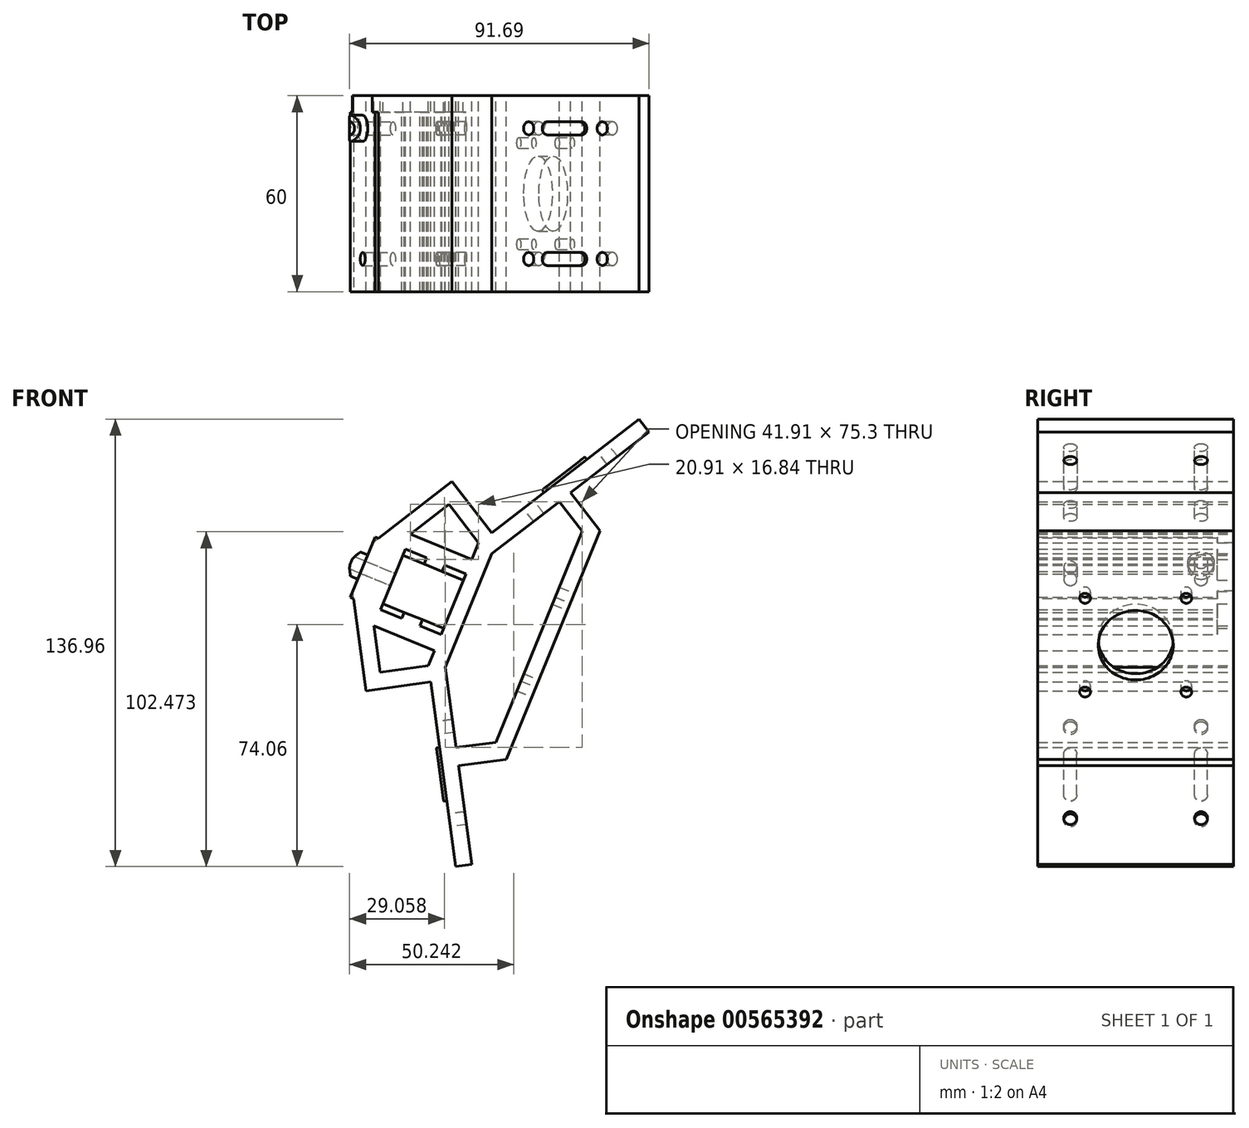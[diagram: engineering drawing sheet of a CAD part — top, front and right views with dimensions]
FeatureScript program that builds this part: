
annotation { "Feature Type Name" : "Feature", "Feature Type Description" : "" }
export const myFeature = defineFeature(function(context is Context, id is Id, definition is map)
    precondition{}
    {
        {
            var Q0;
            Q0=qCreatedBy(makeId("Front.planeOp"),FACE);
            var sketch = newSketch(context, id + "F0", { "sketchPlane" : qUnion([Q0])});
            skLineSegment(sketch, "E0", {"start": v(-32.47, 25.35) * mm, "end": v(-0.83, 49.82) * mm});
            skLineSegment(sketch, "E1", {"start": v(-0.83, 49.82) * mm, "end": v(11.4, 34) * mm});
            skLineSegment(sketch, "E2", {"start": v(-7.28, -11.6) * mm, "end": v(-27.1, -14.29) * mm});
            skLineSegment(sketch, "E3", {"start": v(-27.1, -14.29) * mm, "end": v(-32.47, 25.35) * mm});
            skLineSegment(sketch, "E4", {"start": v(11.4, 34) * mm, "end": v(56.5, 68.87) * mm});
            skLineSegment(sketch, "E5", {"start": v(56.5, 68.87) * mm, "end": v(59.56, 64.91) * mm});
            skLineSegment(sketch, "E6", {"start": v(59.56, 64.91) * mm, "end": v(11.4, 27.68) * mm});
            skLineSegment(sketch, "E7", {"start": v(11.4, 27.68) * mm, "end": v(-2.84, -7.1) * mm});
            skLineSegment(sketch, "E8", {"start": v(-2.84, -7.1) * mm, "end": v(5.33, -67.42) * mm});
            skLineSegment(sketch, "E9", {"start": v(5.33, -67.42) * mm, "end": v(0.37, -68.09) * mm});
            skLineSegment(sketch, "E10", {"start": v(0.37, -68.09) * mm, "end": v(-7.28, -11.6) * mm});
            skPoint(sketch, "E11", {"position": v(35.48, 46.3) * mm});
            skPoint(sketch, "E12", {"position": v(1.24, -37.26) * mm});
            skLineSegment(sketch, "E13", {"start": v(35.48, 46.3) * mm, "end": v(44.51, 34.62) * mm});
            skLineSegment(sketch, "E14", {"start": v(44.51, 34.62) * mm, "end": v(15.87, -35.28) * mm});
            skLineSegment(sketch, "E15", {"start": v(15.87, -35.28) * mm, "end": v(1.24, -37.26) * mm});
            skLineSegment(sketch, "E16", {"start": v(12.61, -30.04) * mm, "end": v(39.07, 34.52) * mm});
            skLineSegment(sketch, "E17", {"start": v(3.45, 21.44) * mm, "end": v(-15.06, 29.02) * mm});
            skLineSegment(sketch, "E18", {"start": v(-15.06, 29.02) * mm, "end": v(-22.64, 10.51) * mm});
            skLineSegment(sketch, "E19", {"start": v(-22.64, 10.51) * mm, "end": v(-4.14, 2.93) * mm});
            skLineSegment(sketch, "E20", {"start": v(-4.14, 2.93) * mm, "end": v(3.45, 21.44) * mm});
            skLineSegment(sketch, "E21", {"start": v(39.07, 34.52) * mm, "end": v(32.03, 43.62) * mm});
            skLineSegment(sketch, "E22", {"start": v(12.61, -30.04) * mm, "end": v(0.49, -31.68) * mm});
            skPoint(sketch, "E23", {"position": v(4.28, 10.29) * mm});
            skPoint(sketch, "E24", {"position": v(-0.34, 12.18) * mm});
            skLineSegment(sketch, "E25", {"start": v(4.28, 10.29) * mm, "end": v(-0.34, 12.18) * mm});
            skLineSegment(sketch, "E26", {"start": v(2.7, 19.59) * mm, "end": v(-15.82, 27.17) * mm});
            skLineSegment(sketch, "E27", {"start": v(-3.38, 4.78) * mm, "end": v(-21.88, 12.37) * mm});
            skLineSegment(sketch, "E28", {"start": v(-10.61, 5.59) * mm, "end": v(-9.85, 7.44) * mm});
            skLineSegment(sketch, "E29", {"start": v(-16.16, 7.86) * mm, "end": v(-15.4, 9.71) * mm});
            skLineSegment(sketch, "E30", {"start": v(-9.34, 24.52) * mm, "end": v(-8.58, 26.37) * mm});
            skPoint(sketch, "E31", {"position": v(-13.39, 6.72) * mm});
            skPoint(sketch, "E32", {"position": v(-5.8, 25.23) * mm});
            skLineSegment(sketch, "E33", {"start": v(-3.79, 22.24) * mm, "end": v(-3.03, 24.1) * mm});
            skLineSegment(sketch, "E34", {"start": v(-1.72, 42.8) * mm, "end": v(7.38, 31.03) * mm});
            skLineSegment(sketch, "E35", {"start": v(7.38, 31.03) * mm, "end": v(5.3, 25.96) * mm});
            skLineSegment(sketch, "E36", {"start": v(5.3, 25.96) * mm, "end": v(-13.52, 33.68) * mm});
            skLineSegment(sketch, "E37", {"start": v(-13.52, 33.68) * mm, "end": v(-1.72, 42.8) * mm});
            skLineSegment(sketch, "E38", {"start": v(-6.19, -2.07) * mm, "end": v(-8.07, -6.67) * mm});
            skLineSegment(sketch, "E39", {"start": v(-8.07, -6.67) * mm, "end": v(-22.81, -8.66) * mm});
            skLineSegment(sketch, "E40", {"start": v(-22.81, -8.66) * mm, "end": v(-24.74, 5.53) * mm});
            skPoint(sketch, "E40.endSnap0", {"position": v(-29.78, 5.53) * mm});
            skLineSegment(sketch, "E41", {"start": v(-24.74, 5.53) * mm, "end": v(-6.19, -2.07) * mm});
            skSolve(sketch);
        }
        {
            var Q0;
            Q0=makeQuery(id+"F0.imprint","IMPRINT",FACE,{"disambiguationData":[TD([[makeQuery(id+"F0.imprint","IMPRINT",EDGE,{"derivedFrom":sQuery(id+"F0.wireOp",EDGE,"E0")}),-1.0]])]});
            var Q1;
            {var subQ0=sQuery(id+"F0.wireOp",EDGE,"E30");Q1=makeQuery(id+"F0.imprint","IMPRINT",FACE,{"disambiguationData":[TD([[makeQuery(id+"F0.imprint","IMPRINT",EDGE,{"derivedFrom":subQ0}),-1.0]])]});}
            var Q2;
            {var subQ0=sQuery(id+"F0.wireOp",EDGE,"E28");Q2=makeQuery(id+"F0.imprint","IMPRINT",FACE,{"disambiguationData":[TD([[makeQuery(id+"F0.imprint","IMPRINT",EDGE,{"derivedFrom":subQ0}),1.0]])]});}
            var Q3;
            {var subQ0=sQuery(id+"F0.wireOp",EDGE,"E13");Q3=makeQuery(id+"F0.imprint","IMPRINT",FACE,{"disambiguationData":[TD([[makeQuery(id+"F0.imprint","IMPRINT",EDGE,{"derivedFrom":subQ0}),-1.0]])]});}
            extrude(context, id + "F1", {"entities" : qUnion([Q0, Q1, Q2, Q3]), "depth" : 60 * mm, "offsetDistance" : 25 * mm});
        }
        {
            var Q0;
            {var subQ3=sQuery(id+"F0.wireOp",EDGE,"E28");Q0=makeQuery(id+"F0.imprint","IMPRINT",FACE,{"disambiguationData":[TD([[makeQuery(id+"F0.imprint","IMPRINT",EDGE,{"derivedFrom":subQ3}),-1.0]])]});}
            var Q1;
            {var subQ5=sQuery(id+"F0.wireOp",EDGE,"E29");Q1=makeQuery(id+"F0.imprint","IMPRINT",FACE,{"disambiguationData":[TD([[makeQuery(id+"F0.imprint","IMPRINT",EDGE,{"derivedFrom":subQ5}),1.0]])]});}
            var Q2;
            {var subQ3=sQuery(id+"F0.wireOp",EDGE,"E30");Q2=makeQuery(id+"F0.imprint","IMPRINT",FACE,{"disambiguationData":[TD([[makeQuery(id+"F0.imprint","IMPRINT",EDGE,{"derivedFrom":subQ3}),1.0]])]});}
            var Q3;
            {var subQ3=sQuery(id+"F0.wireOp",EDGE,"E33");Q3=makeQuery(id+"F0.imprint","IMPRINT",FACE,{"disambiguationData":[TD([[makeQuery(id+"F0.imprint","IMPRINT",EDGE,{"derivedFrom":subQ3}),-1.0]])]});}
            extrude(context, id + "F2", {"entities" : qUnion([Q0, Q1, Q2, Q3]), "operationType" : NewBodyOperationType.ADD, "depth" : 5 * mm, "offsetDistance" : 25 * mm});
        }
        {
            var Q0;
            Q0=makeQuery(id+"F1.opExtrude","SWEPT_FACE",FACE,{"disambiguationData":[OSD([sQuery(id+"F0.wireOp",EDGE,"E14")])]});
            var sketch = newSketch(context, id + "F3", { "sketchPlane" : qUnion([Q0])});
            skCircle(sketch, "E42", {"center": v(-30, 11.14) * mm, "radius": 11.5 * mm});
            skCircle(sketch, "E43", {"center": v(-45.5, 26.64) * mm, "radius": 1.65 * mm});
            skCircle(sketch, "E44", {"center": v(-45.5, -4.36) * mm, "radius": 1.65 * mm});
            skCircle(sketch, "E45", {"center": v(-14.5, -4.36) * mm, "radius": 1.65 * mm});
            skCircle(sketch, "E46", {"center": v(-14.5, 26.64) * mm, "radius": 1.65 * mm});
            skSolve(sketch);
        }
        {
            var Q0;
            Q0=makeQuery(id+"F3.imprint","IMPRINT",FACE,{"disambiguationData":[TD([[makeQuery(id+"F3.imprint","IMPRINT",EDGE,{"derivedFrom":sQuery(id+"F3.wireOp",EDGE,"E42")}),1.0]])]});
            extrude(context, id + "F4", {"entities" : qUnion([Q0]), "operationType" : NewBodyOperationType.REMOVE, "oppositeDirection" : true, "depth" : 5 * mm, "offsetDistance" : 25 * mm});
        }
        {
            var Q0;
            Q0=makeQuery(id+"F3.imprint","IMPRINT",FACE,{"disambiguationData":[TD([[makeQuery(id+"F3.imprint","IMPRINT",EDGE,{"derivedFrom":sQuery(id+"F3.wireOp",EDGE,"E44")}),1.0]])]});
            var Q1;
            Q1=makeQuery(id+"F3.imprint","IMPRINT",FACE,{"disambiguationData":[TD([[makeQuery(id+"F3.imprint","IMPRINT",EDGE,{"derivedFrom":sQuery(id+"F3.wireOp",EDGE,"E43")}),1.0]])]});
            var Q2;
            Q2=makeQuery(id+"F3.imprint","IMPRINT",FACE,{"disambiguationData":[TD([[makeQuery(id+"F3.imprint","IMPRINT",EDGE,{"derivedFrom":sQuery(id+"F3.wireOp",EDGE,"E46")}),1.0]])]});
            var Q3;
            Q3=makeQuery(id+"F3.imprint","IMPRINT",FACE,{"disambiguationData":[TD([[makeQuery(id+"F3.imprint","IMPRINT",EDGE,{"derivedFrom":sQuery(id+"F3.wireOp",EDGE,"E45")}),1.0]])]});
            extrude(context, id + "F5", {"entities" : qUnion([Q0, Q1, Q2, Q3]), "operationType" : NewBodyOperationType.REMOVE, "oppositeDirection" : true, "depth" : 5 * mm, "offsetDistance" : 25 * mm});
        }
        {
            var Q0;
            Q0=makeQuery(id+"F1.opExtrude","SWEPT_EDGE",EDGE,{"disambiguationData":[OSD([sQuery(id+"F0.wireOp",EDGE,"E0"),sQuery(id+"F0.wireOp",EDGE,"E3")])]});
            fillet(context, id + "F6", {"entities" : qUnion([Q0]), "radius" : 5 * mm, "tangentPropagation" : true, "allowEdgeOverflow" : false});
        }
        {
            var Q0;
            Q0=makeQuery(id+"F1.opExtrude","SWEPT_FACE",FACE,{"disambiguationData":[OSD([sQuery(id+"F0.wireOp",EDGE,"E10")])]});
            var sketch = newSketch(context, id + "F7", { "sketchPlane" : qUnion([Q0])});
            skCircle(sketch, "E47", {"center": v(10, -53.27) * mm, "radius": 2 * mm});
            skCircle(sketch, "E48", {"center": v(10, -24.77) * mm, "radius": 2 * mm});
            skCircle(sketch, "E49", {"center": v(50, -24.78) * mm, "radius": 2 * mm});
            skCircle(sketch, "E50", {"center": v(50, -53.27) * mm, "radius": 2 * mm});
            skLineSegment(sketch, "E51", {"start": v(12, -53.27) * mm, "end": v(12, -24.77) * mm});
            skLineSegment(sketch, "E52", {"start": v(8, -53.27) * mm, "end": v(8, -24.77) * mm});
            skCircle(sketch, "E53", {"center": v(10, -45.27) * mm, "radius": 2 * mm});
            skCircle(sketch, "E54", {"center": v(10, -32.77) * mm, "radius": 2 * mm});
            skLineSegment(sketch, "E55", {"start": v(48, -53.27) * mm, "end": v(48, -24.78) * mm});
            skLineSegment(sketch, "E56", {"start": v(52, -53.27) * mm, "end": v(52, -24.78) * mm});
            skCircle(sketch, "E57", {"center": v(50, -45.27) * mm, "radius": 2 * mm});
            skCircle(sketch, "E58", {"center": v(50, -32.78) * mm, "radius": 2 * mm});
            skSolve(sketch);
        }
        {
            var Q0;
            Q0=makeQuery(id+"F7.imprint","IMPRINT",FACE,{"disambiguationData":[TD([[makeQuery(id+"F7.imprint","IMPRINT",EDGE,{"derivedFrom":sQuery(id+"F7.wireOp",EDGE,"E47")}),1.0]])]});
            var Q1;
            Q1=makeQuery(id+"F7.imprint","IMPRINT",FACE,{"disambiguationData":[TD([[makeQuery(id+"F7.imprint","IMPRINT",EDGE,{"derivedFrom":sQuery(id+"F7.wireOp",EDGE,"E50")}),1.0]])]});
            var Q2;
            Q2=makeQuery(id+"F7.imprint","IMPRINT",FACE,{"disambiguationData":[TD([[makeQuery(id+"F7.imprint","IMPRINT",EDGE,{"derivedFrom":sQuery(id+"F7.wireOp",EDGE,"E49")}),1.0]])]});
            var Q3;
            Q3=makeQuery(id+"F7.imprint","IMPRINT",FACE,{"disambiguationData":[TD([[makeQuery(id+"F7.imprint","IMPRINT",EDGE,{"derivedFrom":sQuery(id+"F7.wireOp",EDGE,"E48")}),1.0]])]});
            extrude(context, id + "F8", {"entities" : qUnion([Q0, Q1, Q2, Q3]), "operationType" : NewBodyOperationType.REMOVE, "oppositeDirection" : true, "depth" : 5 * mm, "offsetDistance" : 25 * mm});
        }
        {
            var Q0;
            {var subQ0=sQuery(id+"F7.wireOp",EDGE,"E57");var subQ1=makeQuery(id+"F7.imprint","INTERSECT",VERTEX,{"derivedFrom":[sQuery(id+"F7.wireOp",EDGE,"E55"),subQ0]});Q0=makeQuery(id+"F7.imprint","IMPRINT",FACE,{"disambiguationData":[TD([[makeQuery(id+"F7.imprint","IMPRINT",EDGE,{"disambiguationData":[TD([[subQ1,1.0]])],"derivedFrom":subQ0}),1.0]])]});}
            var Q1;
            {var subQ0=sQuery(id+"F7.wireOp",EDGE,"E57");var subQ1=sQuery(id+"F7.wireOp",EDGE,"E55");var subQ2=makeQuery(id+"F7.imprint","INTERSECT",VERTEX,{"derivedFrom":[subQ1,subQ0]});Q1=makeQuery(id+"F7.imprint","IMPRINT",FACE,{"disambiguationData":[TD([[makeQuery(id+"F7.imprint","IMPRINT",EDGE,{"disambiguationData":[TD([[subQ2,-1.0]])],"derivedFrom":subQ1}),-1.0]])]});}
            var Q2;
            {var subQ0=sQuery(id+"F7.wireOp",EDGE,"E58");var subQ1=makeQuery(id+"F7.imprint","INTERSECT",VERTEX,{"derivedFrom":[sQuery(id+"F7.wireOp",EDGE,"E55"),subQ0]});Q2=makeQuery(id+"F7.imprint","IMPRINT",FACE,{"disambiguationData":[TD([[makeQuery(id+"F7.imprint","IMPRINT",EDGE,{"disambiguationData":[TD([[subQ1,1.0]])],"derivedFrom":subQ0}),1.0]])]});}
            var Q3;
            {var subQ0=sQuery(id+"F7.wireOp",EDGE,"E53");var subQ1=sQuery(id+"F7.wireOp",EDGE,"E51");var subQ2=makeQuery(id+"F7.imprint","INTERSECT",VERTEX,{"derivedFrom":[subQ1,subQ0]});Q3=makeQuery(id+"F7.imprint","IMPRINT",FACE,{"disambiguationData":[TD([[makeQuery(id+"F7.imprint","IMPRINT",EDGE,{"disambiguationData":[TD([[subQ2,-1.0]])],"derivedFrom":subQ1}),1.0]])]});}
            var Q4;
            {var subQ0=sQuery(id+"F7.wireOp",EDGE,"E54");var subQ1=makeQuery(id+"F7.imprint","INTERSECT",VERTEX,{"derivedFrom":[sQuery(id+"F7.wireOp",EDGE,"E51"),subQ0]});Q4=makeQuery(id+"F7.imprint","IMPRINT",FACE,{"disambiguationData":[TD([[makeQuery(id+"F7.imprint","IMPRINT",EDGE,{"disambiguationData":[TD([[subQ1,-1.0]])],"derivedFrom":subQ0}),1.0]])]});}
            var Q5;
            {var subQ0=sQuery(id+"F7.wireOp",EDGE,"E53");var subQ1=makeQuery(id+"F7.imprint","INTERSECT",VERTEX,{"derivedFrom":[sQuery(id+"F7.wireOp",EDGE,"E51"),subQ0]});Q5=makeQuery(id+"F7.imprint","IMPRINT",FACE,{"disambiguationData":[TD([[makeQuery(id+"F7.imprint","IMPRINT",EDGE,{"disambiguationData":[TD([[subQ1,-1.0]])],"derivedFrom":subQ0}),1.0]])]});}
            extrude(context, id + "F9", {"entities" : qUnion([Q0, Q1, Q2, Q3, Q4, Q5]), "operationType" : NewBodyOperationType.ADD, "depth" : 1 * mm, "offsetDistance" : 25 * mm});
        }
        {
            var Q0;
            Q0=makeQuery(id+"F1.opExtrude","SWEPT_FACE",FACE,{"disambiguationData":[OSD([sQuery(id+"F0.wireOp",EDGE,"E4")])]});
            var sketch = newSketch(context, id + "F10", { "sketchPlane" : qUnion([Q0])});
            skCircle(sketch, "E59", {"center": v(44.07, -10) * mm, "radius": 2 * mm});
            skCircle(sketch, "E60", {"center": v(72.57, -10) * mm, "radius": 2 * mm});
            skCircle(sketch, "E61", {"center": v(72.57, -50) * mm, "radius": 2 * mm});
            skCircle(sketch, "E62", {"center": v(44.07, -50) * mm, "radius": 2 * mm});
            skLineSegment(sketch, "E63", {"start": v(44.07, -12) * mm, "end": v(72.57, -12) * mm});
            skLineSegment(sketch, "E64", {"start": v(72.57, -48) * mm, "end": v(44.07, -48) * mm});
            skLineSegment(sketch, "E65", {"start": v(44.07, -8) * mm, "end": v(72.57, -8) * mm});
            skLineSegment(sketch, "E66", {"start": v(44.07, -52) * mm, "end": v(72.57, -52) * mm});
            skCircle(sketch, "E67", {"center": v(52.07, -10) * mm, "radius": 2 * mm});
            skCircle(sketch, "E68", {"center": v(64.57, -10) * mm, "radius": 2 * mm});
            skCircle(sketch, "E69", {"center": v(52.07, -50) * mm, "radius": 2 * mm});
            skCircle(sketch, "E70", {"center": v(64.57, -50) * mm, "radius": 2 * mm});
            skSolve(sketch);
        }
        {
            var Q0;
            {var subQ0=sQuery(id+"F10.wireOp",EDGE,"E67");var subQ1=sQuery(id+"F10.wireOp",EDGE,"E63");var subQ2=makeQuery(id+"F10.imprint","INTERSECT",VERTEX,{"derivedFrom":[subQ1,subQ0]});Q0=makeQuery(id+"F10.imprint","IMPRINT",FACE,{"disambiguationData":[TD([[makeQuery(id+"F10.imprint","IMPRINT",EDGE,{"disambiguationData":[TD([[subQ2,-1.0]])],"derivedFrom":subQ1}),1.0]])]});}
            var Q1;
            {var subQ0=sQuery(id+"F10.wireOp",EDGE,"E67");var subQ1=makeQuery(id+"F10.imprint","INTERSECT",VERTEX,{"derivedFrom":[sQuery(id+"F10.wireOp",EDGE,"E63"),subQ0]});Q1=makeQuery(id+"F10.imprint","IMPRINT",FACE,{"disambiguationData":[TD([[makeQuery(id+"F10.imprint","IMPRINT",EDGE,{"disambiguationData":[TD([[subQ1,1.0]])],"derivedFrom":subQ0}),1.0]])]});}
            var Q2;
            {var subQ0=sQuery(id+"F10.wireOp",EDGE,"E68");var subQ1=makeQuery(id+"F10.imprint","INTERSECT",VERTEX,{"derivedFrom":[sQuery(id+"F10.wireOp",EDGE,"E63"),subQ0]});Q2=makeQuery(id+"F10.imprint","IMPRINT",FACE,{"disambiguationData":[TD([[makeQuery(id+"F10.imprint","IMPRINT",EDGE,{"disambiguationData":[TD([[subQ1,1.0]])],"derivedFrom":subQ0}),1.0]])]});}
            var Q3;
            {var subQ0=sQuery(id+"F10.wireOp",EDGE,"E69");var subQ1=makeQuery(id+"F10.imprint","INTERSECT",VERTEX,{"derivedFrom":[sQuery(id+"F10.wireOp",EDGE,"E64"),subQ0]});Q3=makeQuery(id+"F10.imprint","IMPRINT",FACE,{"disambiguationData":[TD([[makeQuery(id+"F10.imprint","IMPRINT",EDGE,{"disambiguationData":[TD([[subQ1,-1.0]])],"derivedFrom":subQ0}),1.0]])]});}
            var Q4;
            {var subQ0=sQuery(id+"F10.wireOp",EDGE,"E70");var subQ1=sQuery(id+"F10.wireOp",EDGE,"E64");var subQ2=makeQuery(id+"F10.imprint","INTERSECT",VERTEX,{"derivedFrom":[subQ1,subQ0]});Q4=makeQuery(id+"F10.imprint","IMPRINT",FACE,{"disambiguationData":[TD([[makeQuery(id+"F10.imprint","IMPRINT",EDGE,{"disambiguationData":[TD([[subQ2,-1.0]])],"derivedFrom":subQ1}),1.0]])]});}
            var Q5;
            {var subQ0=sQuery(id+"F10.wireOp",EDGE,"E70");var subQ1=makeQuery(id+"F10.imprint","INTERSECT",VERTEX,{"derivedFrom":[sQuery(id+"F10.wireOp",EDGE,"E64"),subQ0]});Q5=makeQuery(id+"F10.imprint","IMPRINT",FACE,{"disambiguationData":[TD([[makeQuery(id+"F10.imprint","IMPRINT",EDGE,{"disambiguationData":[TD([[subQ1,-1.0]])],"derivedFrom":subQ0}),1.0]])]});}
            extrude(context, id + "F11", {"entities" : qUnion([Q0, Q1, Q2, Q3, Q4, Q5]), "operationType" : NewBodyOperationType.ADD, "depth" : 1 * mm, "offsetDistance" : 25 * mm});
        }
        {
            var Q0;
            {var subQ0=sQuery(id+"F10.wireOp",EDGE,"E59");var subQ1=makeQuery(id+"F10.imprint","INTERSECT",VERTEX,{"derivedFrom":[subQ0,sQuery(id+"F10.wireOp",EDGE,"E63")]});Q0=makeQuery(id+"F10.imprint","IMPRINT",FACE,{"disambiguationData":[TD([[makeQuery(id+"F10.imprint","IMPRINT",EDGE,{"disambiguationData":[TD([[subQ1,1.0]])],"derivedFrom":subQ0}),1.0]])]});}
            var Q1;
            {var subQ0=sQuery(id+"F10.wireOp",EDGE,"E60");var subQ1=makeQuery(id+"F10.imprint","INTERSECT",VERTEX,{"derivedFrom":[subQ0,sQuery(id+"F10.wireOp",EDGE,"E63")]});Q1=makeQuery(id+"F10.imprint","IMPRINT",FACE,{"disambiguationData":[TD([[makeQuery(id+"F10.imprint","IMPRINT",EDGE,{"disambiguationData":[TD([[subQ1,1.0]])],"derivedFrom":subQ0}),1.0]])]});}
            var Q2;
            {var subQ0=sQuery(id+"F10.wireOp",EDGE,"E62");var subQ1=makeQuery(id+"F10.imprint","INTERSECT",VERTEX,{"derivedFrom":[subQ0,sQuery(id+"F10.wireOp",EDGE,"E64")]});Q2=makeQuery(id+"F10.imprint","IMPRINT",FACE,{"disambiguationData":[TD([[makeQuery(id+"F10.imprint","IMPRINT",EDGE,{"disambiguationData":[TD([[subQ1,-1.0]])],"derivedFrom":subQ0}),1.0]])]});}
            var Q3;
            {var subQ0=sQuery(id+"F10.wireOp",EDGE,"E61");var subQ1=makeQuery(id+"F10.imprint","INTERSECT",VERTEX,{"derivedFrom":[subQ0,sQuery(id+"F10.wireOp",EDGE,"E64")]});Q3=makeQuery(id+"F10.imprint","IMPRINT",FACE,{"disambiguationData":[TD([[makeQuery(id+"F10.imprint","IMPRINT",EDGE,{"disambiguationData":[TD([[subQ1,-1.0]])],"derivedFrom":subQ0}),1.0]])]});}
            extrude(context, id + "F12", {"entities" : qUnion([Q0, Q1, Q2, Q3]), "operationType" : NewBodyOperationType.REMOVE, "oppositeDirection" : true, "depth" : 5 * mm, "offsetDistance" : 25 * mm});
        }
        {
            var Q0;
            Q0=makeQuery(id+"F1.opExtrude","SWEPT_FACE",FACE,{"disambiguationData":[OSD([sQuery(id+"F0.wireOp",EDGE,"E18")])]});
            var sketch = newSketch(context, id + "F13", { "sketchPlane" : qUnion([Q0])});
            skLineSegment(sketch, "E71", {"start": v(0, 11.14) * mm, "end": v(-60, 11.14) * mm});
            skCircle(sketch, "E72", {"center": v(-10, 11.14) * mm, "radius": 2 * mm});
            skCircle(sketch, "E73", {"center": v(-50, 11.14) * mm, "radius": 2 * mm});
            skCircle(sketch, "E74", {"center": v(-10, 11.14) * mm, "radius": 4 * mm});
            skCircle(sketch, "E75", {"center": v(-50, 11.14) * mm, "radius": 4 * mm});
            skSolve(sketch);
        }
        {
            var Q0;
            {var subQ0=sQuery(id+"F13.wireOp",EDGE,"E73");var subQ1=sQuery(id+"F13.wireOp",EDGE,"E71");var subQ2=makeQuery(id+"F13.imprint","INTERSECT",VERTEX,{"disambiguationData":[OD(0.0)],"derivedFrom":[subQ1,subQ0]});Q0=makeQuery(id+"F13.imprint","IMPRINT",FACE,{"disambiguationData":[TD([[makeQuery(id+"F13.imprint","IMPRINT",EDGE,{"disambiguationData":[TD([[subQ2,-1.0]])],"derivedFrom":subQ1}),1.0]])]});}
            var Q1;
            {var subQ0=sQuery(id+"F13.wireOp",EDGE,"E73");var subQ1=sQuery(id+"F13.wireOp",EDGE,"E71");var subQ2=makeQuery(id+"F13.imprint","INTERSECT",VERTEX,{"disambiguationData":[OD(0.0)],"derivedFrom":[subQ1,subQ0]});Q1=makeQuery(id+"F13.imprint","IMPRINT",FACE,{"disambiguationData":[TD([[makeQuery(id+"F13.imprint","IMPRINT",EDGE,{"disambiguationData":[TD([[subQ2,-1.0]])],"derivedFrom":subQ1}),-1.0]])]});}
            var Q2;
            {var subQ0=sQuery(id+"F13.wireOp",EDGE,"E72");var subQ1=sQuery(id+"F13.wireOp",EDGE,"E71");var subQ2=makeQuery(id+"F13.imprint","INTERSECT",VERTEX,{"disambiguationData":[OD(0.0)],"derivedFrom":[subQ1,subQ0]});Q2=makeQuery(id+"F13.imprint","IMPRINT",FACE,{"disambiguationData":[TD([[makeQuery(id+"F13.imprint","IMPRINT",EDGE,{"disambiguationData":[TD([[subQ2,-1.0]])],"derivedFrom":subQ1}),1.0]])]});}
            var Q3;
            {var subQ0=sQuery(id+"F13.wireOp",EDGE,"E72");var subQ1=sQuery(id+"F13.wireOp",EDGE,"E71");var subQ2=makeQuery(id+"F13.imprint","INTERSECT",VERTEX,{"disambiguationData":[OD(0.0)],"derivedFrom":[subQ1,subQ0]});Q3=makeQuery(id+"F13.imprint","IMPRINT",FACE,{"disambiguationData":[TD([[makeQuery(id+"F13.imprint","IMPRINT",EDGE,{"disambiguationData":[TD([[subQ2,-1.0]])],"derivedFrom":subQ1}),-1.0]])]});}
            extrude(context, id + "F14", {"entities" : qUnion([Q0, Q1, Q2, Q3]), "operationType" : NewBodyOperationType.REMOVE, "oppositeDirection" : true, "depth" : 25 * mm, "offsetDistance" : 25 * mm});
        }
        {
            var Q0;
            {var subQ0=sQuery(id+"F13.wireOp",EDGE,"E75");var subQ1=sQuery(id+"F13.wireOp",EDGE,"E71");var subQ2=makeQuery(id+"F13.imprint","INTERSECT",VERTEX,{"disambiguationData":[OD(0.0)],"derivedFrom":[subQ1,subQ0]});Q0=makeQuery(id+"F13.imprint","IMPRINT",FACE,{"disambiguationData":[TD([[makeQuery(id+"F13.imprint","IMPRINT",EDGE,{"disambiguationData":[TD([[subQ2,-1.0]])],"derivedFrom":subQ1}),1.0]])]});}
            var Q1;
            {var subQ0=sQuery(id+"F13.wireOp",EDGE,"E75");var subQ1=sQuery(id+"F13.wireOp",EDGE,"E71");var subQ2=makeQuery(id+"F13.imprint","INTERSECT",VERTEX,{"disambiguationData":[OD(0.0)],"derivedFrom":[subQ1,subQ0]});Q1=makeQuery(id+"F13.imprint","IMPRINT",FACE,{"disambiguationData":[TD([[makeQuery(id+"F13.imprint","IMPRINT",EDGE,{"disambiguationData":[TD([[subQ2,-1.0]])],"derivedFrom":subQ1}),-1.0]])]});}
            var Q2;
            {var subQ0=sQuery(id+"F13.wireOp",EDGE,"E74");var subQ1=sQuery(id+"F13.wireOp",EDGE,"E71");var subQ2=makeQuery(id+"F13.imprint","INTERSECT",VERTEX,{"disambiguationData":[OD(0.0)],"derivedFrom":[subQ1,subQ0]});Q2=makeQuery(id+"F13.imprint","IMPRINT",FACE,{"disambiguationData":[TD([[makeQuery(id+"F13.imprint","IMPRINT",EDGE,{"disambiguationData":[TD([[subQ2,-1.0]])],"derivedFrom":subQ1}),1.0]])]});}
            var Q3;
            {var subQ0=sQuery(id+"F13.wireOp",EDGE,"E74");var subQ1=sQuery(id+"F13.wireOp",EDGE,"E71");var subQ2=makeQuery(id+"F13.imprint","INTERSECT",VERTEX,{"disambiguationData":[OD(0.0)],"derivedFrom":[subQ1,subQ0]});Q3=makeQuery(id+"F13.imprint","IMPRINT",FACE,{"disambiguationData":[TD([[makeQuery(id+"F13.imprint","IMPRINT",EDGE,{"disambiguationData":[TD([[subQ2,-1.0]])],"derivedFrom":subQ1}),-1.0]])]});}
            extrude(context, id + "F15", {"entities" : qUnion([Q0, Q1, Q2, Q3]), "operationType" : NewBodyOperationType.ADD, "oppositeDirection" : true, "depth" : 20 * mm, "offsetDistance" : 25 * mm});
        }
        {
            var Q0;
            Q0=makeQuery(id+"F15.opExtrude","CAP_FACE",FACE,{"disambiguationData":[OSD([sQuery(id+"F13.wireOp",EDGE,"E72"),sQuery(id+"F13.wireOp",EDGE,"E74")])],"isStart":false});
            var Q1;
            Q1=makeQuery(id+"F15.opExtrude","CAP_FACE",FACE,{"disambiguationData":[OSD([sQuery(id+"F13.wireOp",EDGE,"E73"),sQuery(id+"F13.wireOp",EDGE,"E75")])],"isStart":false});
            extrude(context, id + "F16", {"entities" : qUnion([Q0, Q1]), "operationType" : NewBodyOperationType.REMOVE, "oppositeDirection" : true, "depth" : 10 * mm, "offsetDistance" : 25 * mm});
        }
    });
